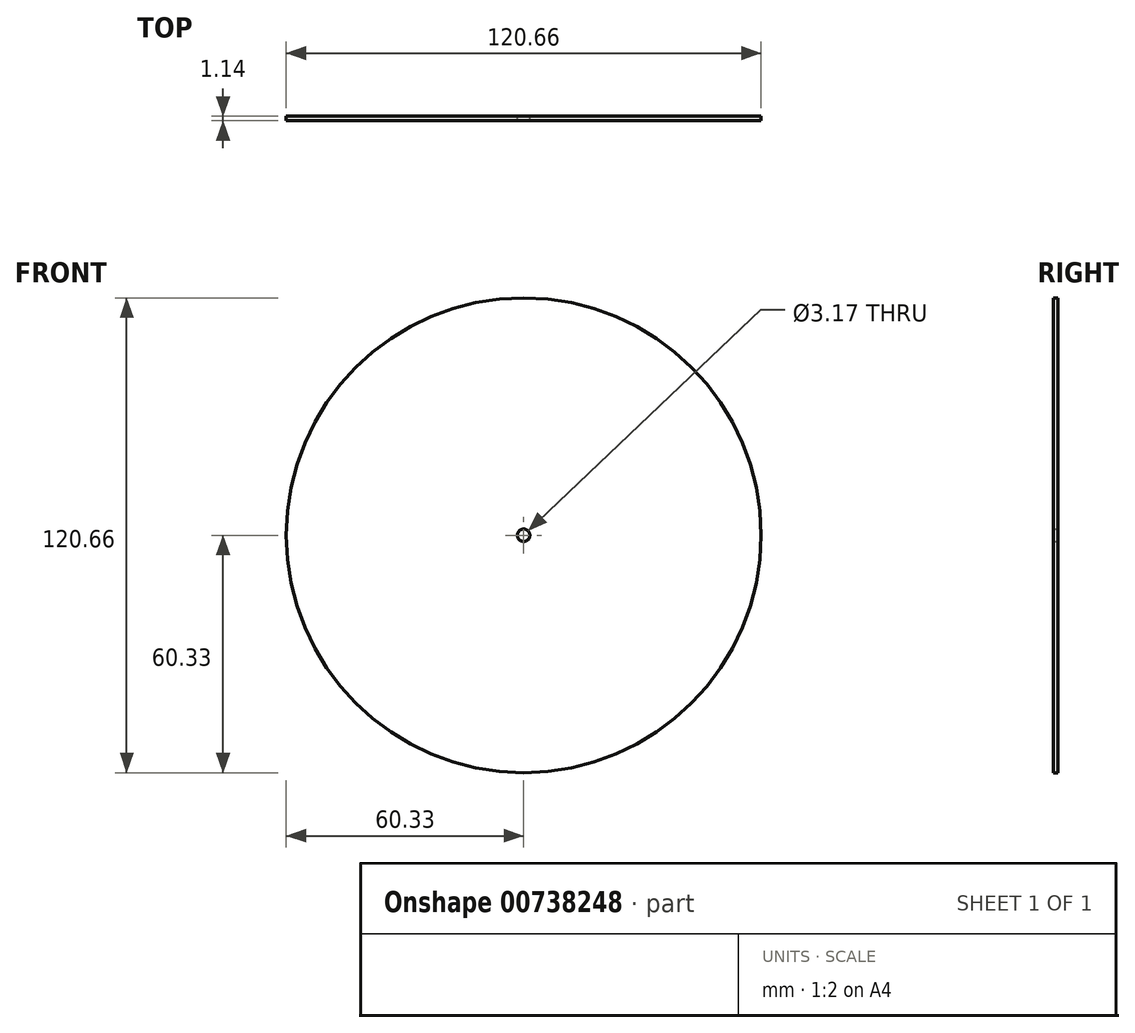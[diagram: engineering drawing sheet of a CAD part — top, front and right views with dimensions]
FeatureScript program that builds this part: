
annotation { "Feature Type Name" : "Feature", "Feature Type Description" : "" }
export const myFeature = defineFeature(function(context is Context, id is Id, definition is map)
    precondition{}
    {
        {
            var Q0;
            Q0=qCreatedBy(makeId("Front.planeOp"),FACE);
            var sketch = newSketch(context, id + "F0", { "sketchPlane" : qUnion([Q0])});
            skCircle(sketch, "E0", {"center": v(0, 0) * mm, "radius": 60.33 * mm});
            skCircle(sketch, "E1", {"center": v(0, 0) * mm, "radius": 1.59 * mm});
            skSolve(sketch);
        }
        {
            var Q0;
            Q0=makeQuery(id+"F0.imprint","IMPRINT",FACE,{"disambiguationData":[TD([[makeQuery(id+"F0.imprint","IMPRINT",EDGE,{"derivedFrom":sQuery(id+"F0.wireOp",EDGE,"UuqY83y2-fal8-4sPw-Gu9t-06vdk2I11vHI")}),1.0]])]});
            var Q1;
            Q1=makeQuery(id+"F0.imprint","IMPRINT",FACE,{"disambiguationData":[TD([[makeQuery(id+"F0.imprint","IMPRINT",EDGE,{"derivedFrom":sQuery(id+"F0.wireOp",EDGE,"E0")}),1.0]])]});
            extrude(context, id + "F1", {"entities" : qUnion([Q0, Q1]), "depth" : 1.14 * mm, "offsetDistance" : 25.4 * mm});
        }
    });
